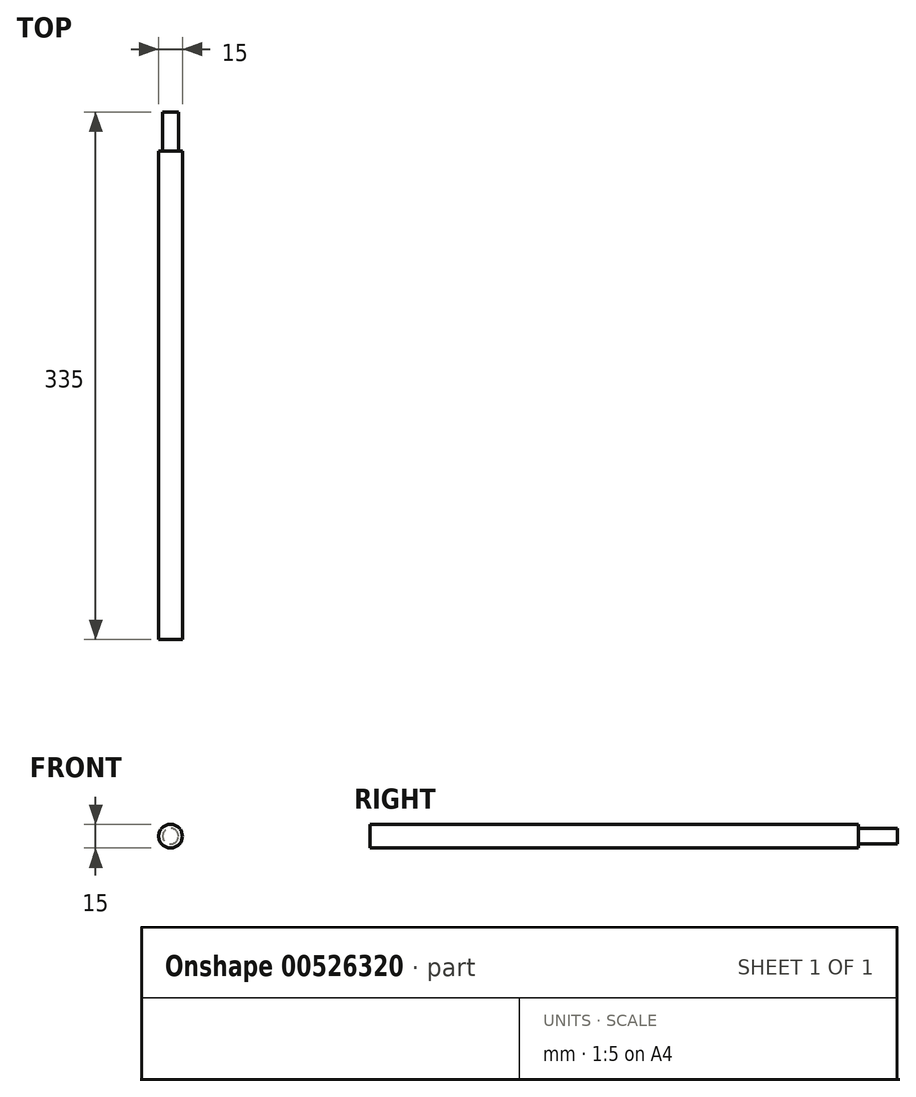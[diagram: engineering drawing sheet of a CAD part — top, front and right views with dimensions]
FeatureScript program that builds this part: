
annotation { "Feature Type Name" : "Feature", "Feature Type Description" : "" }
export const myFeature = defineFeature(function(context is Context, id is Id, definition is map)
    precondition{}
    {
        {
            var Q0;
            Q0=qCreatedBy(makeId("Front.planeOp"),FACE);
            var sketch = newSketch(context, id + "F0", { "sketchPlane" : qUnion([Q0])});
            skCircle(sketch, "E0", {"center": v(0, 0) * mm, "radius": 7.5 * mm});
            skSolve(sketch);
        }
        {
            var Q0;
            Q0 = qSketchRegion(id + "F0", true);
            extrude(context, id + "F1", {"entities" : qUnion([Q0]), "depth" : 310 * mm, "offsetDistance" : 25 * mm});
        }
        {
            var Q0;
            Q0=makeQuery(id+"F1.opExtrude","CAP_FACE",FACE,{"disambiguationData":[OSD([sQuery(id+"F0.wireOp",EDGE,"E0")])],"isStart":true});
            var sketch = newSketch(context, id + "F2", { "sketchPlane" : qUnion([Q0])});
            skCircle(sketch, "E1", {"center": v(0, 0) * mm, "radius": 5 * mm});
            skSolve(sketch);
        }
        {
            var Q0;
            Q0 = qSketchRegion(id + "F2", true);
            extrude(context, id + "F3", {"entities" : qUnion([Q0]), "operationType" : NewBodyOperationType.ADD, "depth" : 25 * mm, "offsetDistance" : 25 * mm});
        }
    });
